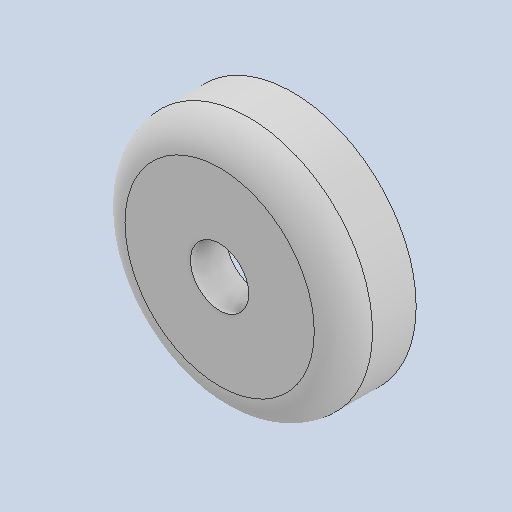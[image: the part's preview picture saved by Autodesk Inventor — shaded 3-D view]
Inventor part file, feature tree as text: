
AUTODESK INVENTOR PART (.ipt)
format: ipt  version: 2022 (Build 260153070, 153G)  size: 141,312 bytes
history: native  units: mm
features: extrude x2, sketch x2, fillet x1
ambient origin geometry x8: Origin, YZ Plane, XZ Plane, XY Plane, X Axis, Y Axis, Z Axis, Center Point
bodies: Solid1 (feature_tree)
feature tree (5):
  extrude  "Extrusion1"  Depth=5.45mm
  extrude  "Extrusion2"  Depth=1.25mm TaperAngle=0.0deg
  fillet  "Fillet1"  Radius=2.0mm
  sketch  "Sketch1"  dims[d0=7.1mm d1=5.45mm]
  sketch  "Sketch4"  dims[d2=8.5mm d3=1.25mm d4=0.0mm d7=2.0mm d8=1.25mm d9=0.0mm d10=1.0mm]
